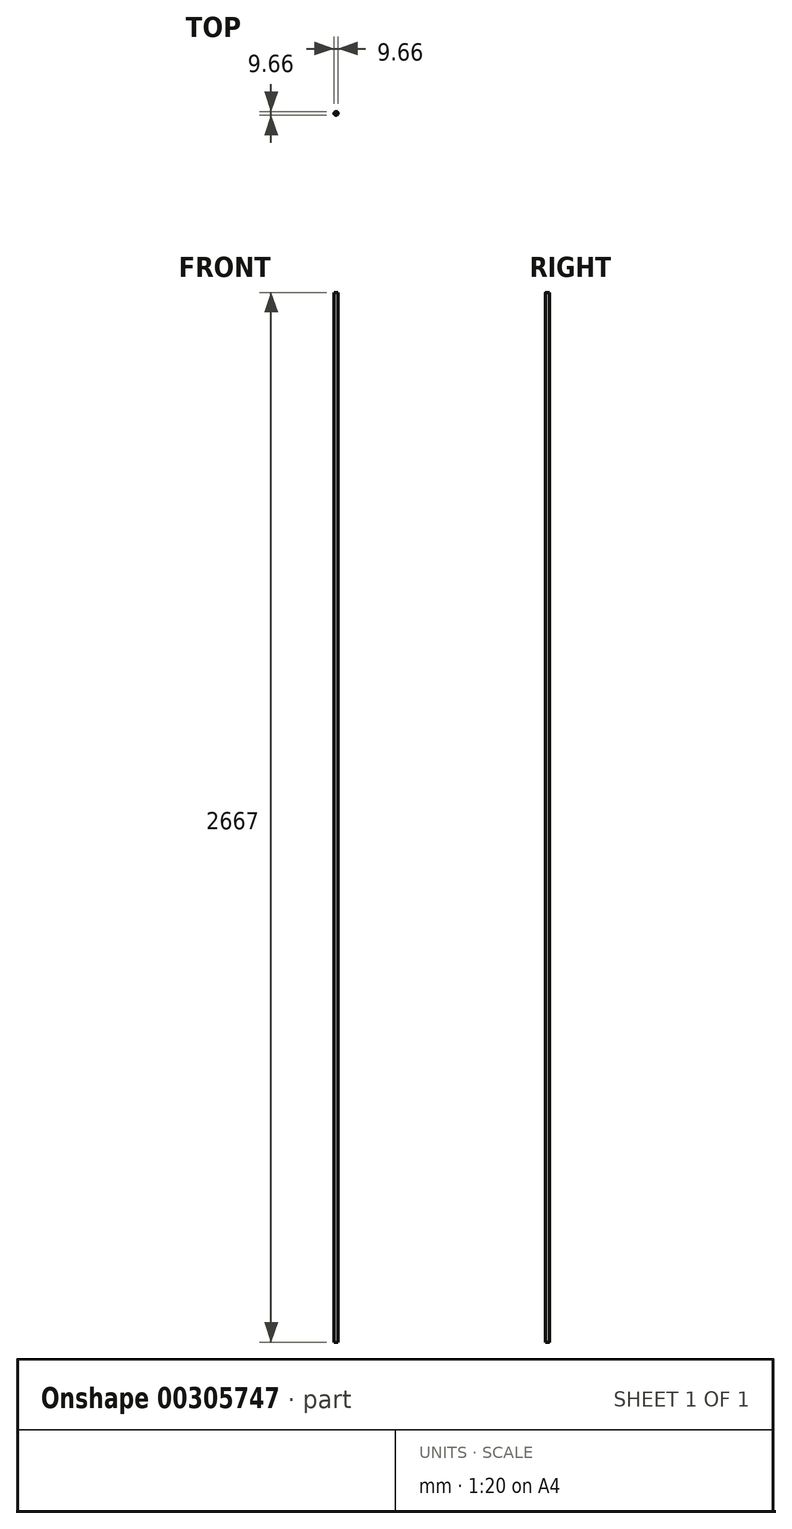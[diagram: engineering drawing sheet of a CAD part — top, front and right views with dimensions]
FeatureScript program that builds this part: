
annotation { "Feature Type Name" : "Feature", "Feature Type Description" : "" }
export const myFeature = defineFeature(function(context is Context, id is Id, definition is map)
    precondition{}
    {
        {
            var Q0;
            Q0=qCreatedBy(makeId("Top.planeOp"),FACE);
            var sketch = newSketch(context, id + "F0", { "sketchPlane" : qUnion([Q0])});
            skCircle(sketch, "E0", {"center": v(0, 0) * mm, "radius": 4.83 * mm});
            skSolve(sketch);
        }
        {
            var Q0;
            Q0 = qSketchRegion(id + "F0", true);
            extrude(context, id + "F1", {"entities" : qUnion([Q0]), "endBound" : BoundingType.SYMMETRIC, "depth" : 2667 * mm});
        }
    });
